# Revit family: Data_Device-Network-Leviton-QuickPort-Angled_Faceplate-4_Port
name_source: partatom
category: Data Devices
units: mm (PartAtom-declared; Revit-internal decimal feet)

## family parameters
Cut with Voids When Loaded = No
Host = Face
Maintain Annotation Orientation = Yes
OmniClass Number = 23.85.50.17
OmniClass Title = Communication and Data Processing Equipment
Part Type = Normal
Room Calculation Point = No
Round Connector Dimension = Use Diameter
Shared = Yes

## types (1)
- 4-Port Universal Angled Faceplate, Color Black
    Assembly Code = D5030600
    Cable Clearance Rear is Visible = Yes
    Date Last Modified = October 04, 2023
    Default Elevation = 24 "
    Depth = 1.595 "
    Description = Universal 4-Port Angled Modular Furniture Faceplate with Labeling Designation Window, black
    Equipment Abbreviation = QPA
    Faceplate Material = Plastic - Leviton - Black
    Family Version = 1.0.0
    Has ID Windows = Yes
    Height = 2.42 "
    Manufacturer = Leviton
    Minimum Order Quantity = 0
    Model Disclaimer = http://www.leviton.com
    Part Description = Universal 4-Port Angled Modular Furniture Faceplate with Labeling Designation Window, black
    Product Documentation Link = https://www.leviton.com
    Quantity per Package = 0
    Shielded = No
    URL = http://www.leviton.com
    Width = 4.094 "
    z Leviton Type = 1
    z Offset 1 = 0.2 "

## geometry (parser evidence)
native form markers: Blend x6, Sweep x5
no freeform markers — native parametric forms only
